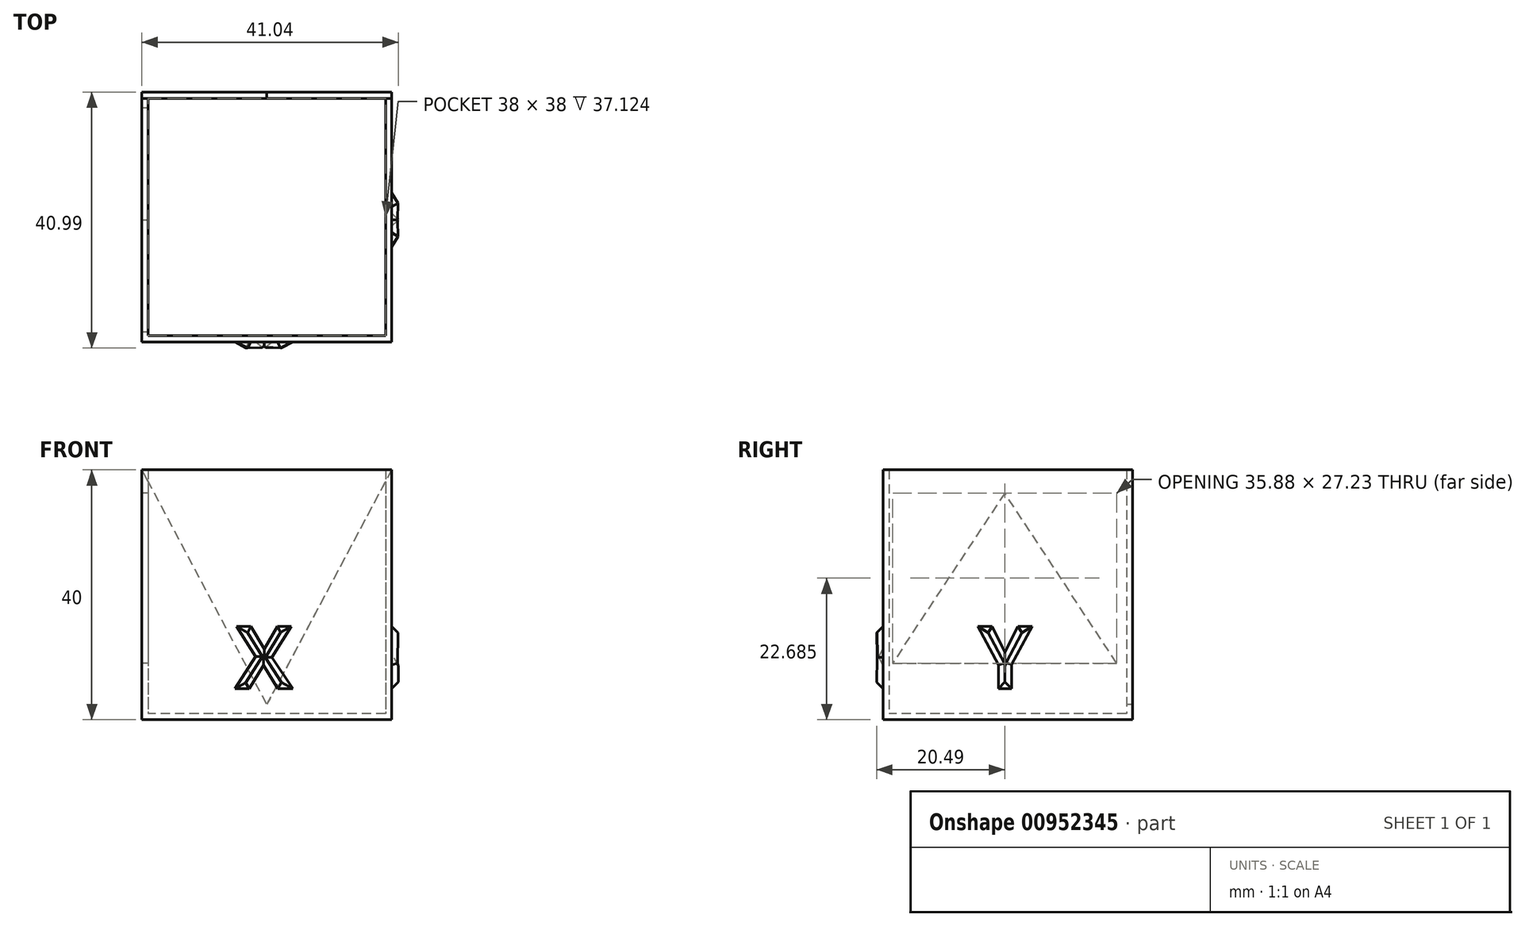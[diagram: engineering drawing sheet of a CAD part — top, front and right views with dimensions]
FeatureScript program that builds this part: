
annotation { "Feature Type Name" : "Feature", "Feature Type Description" : "" }
export const myFeature = defineFeature(function(context is Context, id is Id, definition is map)
    precondition{}
    {
        {
            var Q0;
            Q0=qCreatedBy(makeId("Top.planeOp"),FACE);
            var sketch = newSketch(context, id + "F0", { "sketchPlane" : qUnion([Q0])});
            skLineSegment(sketch, "E0.bottom", {"start": v(20, 20) * mm, "end": v(-20, 20) * mm});
            skLineSegment(sketch, "E0.top", {"start": v(20, -20) * mm, "end": v(-20, -20) * mm});
            skLineSegment(sketch, "E0.left", {"start": v(20, 20) * mm, "end": v(20, -20) * mm});
            skLineSegment(sketch, "E0.right", {"start": v(-20, 20) * mm, "end": v(-20, -20) * mm});
            skPoint(sketch, "E0.middle", {"position": v(0, 0) * mm});
            skSolve(sketch);
        }
        {
            var Q0;
            Q0=makeQuery(id+"F0.imprint","IMPRINT",FACE,{"disambiguationData":[TD([[makeQuery(id+"F0.imprint","IMPRINT",EDGE,{"derivedFrom":sQuery(id+"F0.wireOp",EDGE,"E0.bottom")}),1.0]])]});
            extrude(context, id + "F1", {"entities" : qUnion([Q0]), "depth" : 40 * mm, "offsetDistance" : 25 * mm});
        }
        {
            var Q0;
            Q0=makeQuery(id+"F1.opExtrude","CAP_FACE",FACE,{"disambiguationData":[OSD([sQuery(id+"F0.wireOp",EDGE,"E0.bottom"),sQuery(id+"F0.wireOp",EDGE,"E0.top"),sQuery(id+"F0.wireOp",EDGE,"E0.left"),sQuery(id+"F0.wireOp",EDGE,"E0.right")])],"isStart":false});
            shell(context, id + "F2", {"entities" : qUnion([Q0]), "thickness" : 1 * mm});
        }
        {
            var Q0;
            Q0=makeQuery(id+"F1.opExtrude","SWEPT_FACE",FACE,{"disambiguationData":[OSD([sQuery(id+"F0.wireOp",EDGE,"E0.top")])]});
            var sketch = newSketch(context, id + "F3", { "sketchPlane" : qUnion([Q0])});
            skText(sketch, "E1", { "text": "X", "fontName": "OpenSans-Bold.ttf"});
            const initialGuessF3  = {"E1": [-0.00508, 0.005, 1, 0, 0.01]};
            skSetInitialGuess(sketch, initialGuessF3);
            skSolve(sketch);
        }
        {
            var Q0;
            Q0=makeQuery(id+"F1.opExtrude","SWEPT_FACE",FACE,{"disambiguationData":[OSD([sQuery(id+"F0.wireOp",EDGE,"E0.left")])]});
            var sketch = newSketch(context, id + "F4", { "sketchPlane" : qUnion([Q0])});
            skText(sketch, "E2", { "text": "Y", "fontName": "OpenSans-Bold.ttf"});
            const initialGuessF4  = {"E2": [-0.00478, 0.005, 1, 0, 0.01]};
            skSetInitialGuess(sketch, initialGuessF4);
            skSolve(sketch);
        }
        {
            var Q0;
            Q0 = qSketchRegion(id + "F3", true);
            extrude(context, id + "F5", {"entities" : qUnion([Q0]), "operationType" : NewBodyOperationType.ADD, "depth" : 2 * mm, "offsetDistance" : 25 * mm, "hasDraft" : true, "draftAngle" : 45 * degree, "draftPullDirection" : true});
        }
        {
            var Q0;
            Q0=makeQuery(id+"F4.imprint","IMPRINT",FACE,{"disambiguationData":[TD([[makeQuery(id+"F4.imprint","IMPRINT",EDGE,{"derivedFrom":sQuery(id+"F4.wireOp",EDGE,"E2.sketch_text.stroke-0")}),-1.0]])]});
            extrude(context, id + "F6", {"entities" : qUnion([Q0]), "operationType" : NewBodyOperationType.ADD, "depth" : 2 * mm, "offsetDistance" : 25 * mm, "hasDraft" : true, "draftAngle" : 45 * degree, "draftPullDirection" : true});
        }
        {
            var Q0;
            Q0=makeQuery(id+"F1.opExtrude","SWEPT_FACE",FACE,{"disambiguationData":[OSD([sQuery(id+"F0.wireOp",EDGE,"E0.bottom")])]});
            var sketch = newSketch(context, id + "F7", { "sketchPlane" : qUnion([Q0])});
            skLineSegment(sketch, "E3", {"start": v(-20, 40) * mm, "end": v(0, 2.48) * mm});
            skPoint(sketch, "E3.endSnap0", {"position": v(-20, 20) * mm});
            skLineSegment(sketch, "E4", {"start": v(0, 2.48) * mm, "end": v(20, 40) * mm});
            skLineSegment(sketch, "E5", {"start": v(20, 40) * mm, "end": v(-20, 40) * mm});
            skSolve(sketch);
        }
        {
            var Q0;
            Q0=makeQuery(id+"F7.imprint","IMPRINT",FACE,{"disambiguationData":[TD([[makeQuery(id+"F7.imprint","IMPRINT",EDGE,{"derivedFrom":sQuery(id+"F7.wireOp",EDGE,"E3")}),1.0]])]});
            var Q1;
            Q1=makeQuery(id+"F2.opShell","OFFSET_FACE",FACE,{"disambiguationData":[OSD([sQuery(id+"F0.wireOp",EDGE,"E0.bottom")])]});
            extrude(context, id + "F8", {"entities" : qUnion([Q0]), "operationType" : NewBodyOperationType.REMOVE, "endBound" : BoundingType.UP_TO_SURFACE, "oppositeDirection" : true, "depth" : 25 * mm, "endBoundEntityFace" : qUnion([Q1]), "offsetDistance" : 25 * mm});
        }
        {
            var Q0;
            Q0=makeQuery(id+"F1.opExtrude","SWEPT_FACE",FACE,{"disambiguationData":[OSD([sQuery(id+"F0.wireOp",EDGE,"E0.right")])]});
            var sketch = newSketch(context, id + "F9", { "sketchPlane" : qUnion([Q0])});
            skLineSegment(sketch, "E6", {"start": v(-17.44, 9.07) * mm, "end": v(0.5, 36.3) * mm});
            skLineSegment(sketch, "E7", {"start": v(0.5, 36.3) * mm, "end": v(18.44, 9.07) * mm});
            skLineSegment(sketch, "E8", {"start": v(18.44, 9.07) * mm, "end": v(-17.44, 9.07) * mm});
            skLineSegment(sketch, "E9", {"start": v(0.5, 40) * mm, "end": v(0.5, 0) * mm, "construction": true});
            skPoint(sketch, "E9.endSnap0", {"position": v(0, 0) * mm});
            skSolve(sketch);
        }
        {
            var Q0;
            Q0=makeQuery(id+"F9.imprint","IMPRINT",FACE,{"disambiguationData":[TD([[makeQuery(id+"F9.imprint","IMPRINT",EDGE,{"derivedFrom":sQuery(id+"F9.wireOp",EDGE,"E6")}),-1.0]])]});
            var Q1;
            Q1=makeQuery(id+"F2.opShell","OFFSET_FACE",FACE,{"disambiguationData":[OSD([sQuery(id+"F0.wireOp",EDGE,"E0.right")])]});
            extrude(context, id + "F10", {"entities" : qUnion([Q0]), "operationType" : NewBodyOperationType.REMOVE, "endBound" : BoundingType.UP_TO_SURFACE, "oppositeDirection" : true, "depth" : 25 * mm, "endBoundEntityFace" : qUnion([Q1]), "offsetDistance" : 25 * mm});
        }
    });
